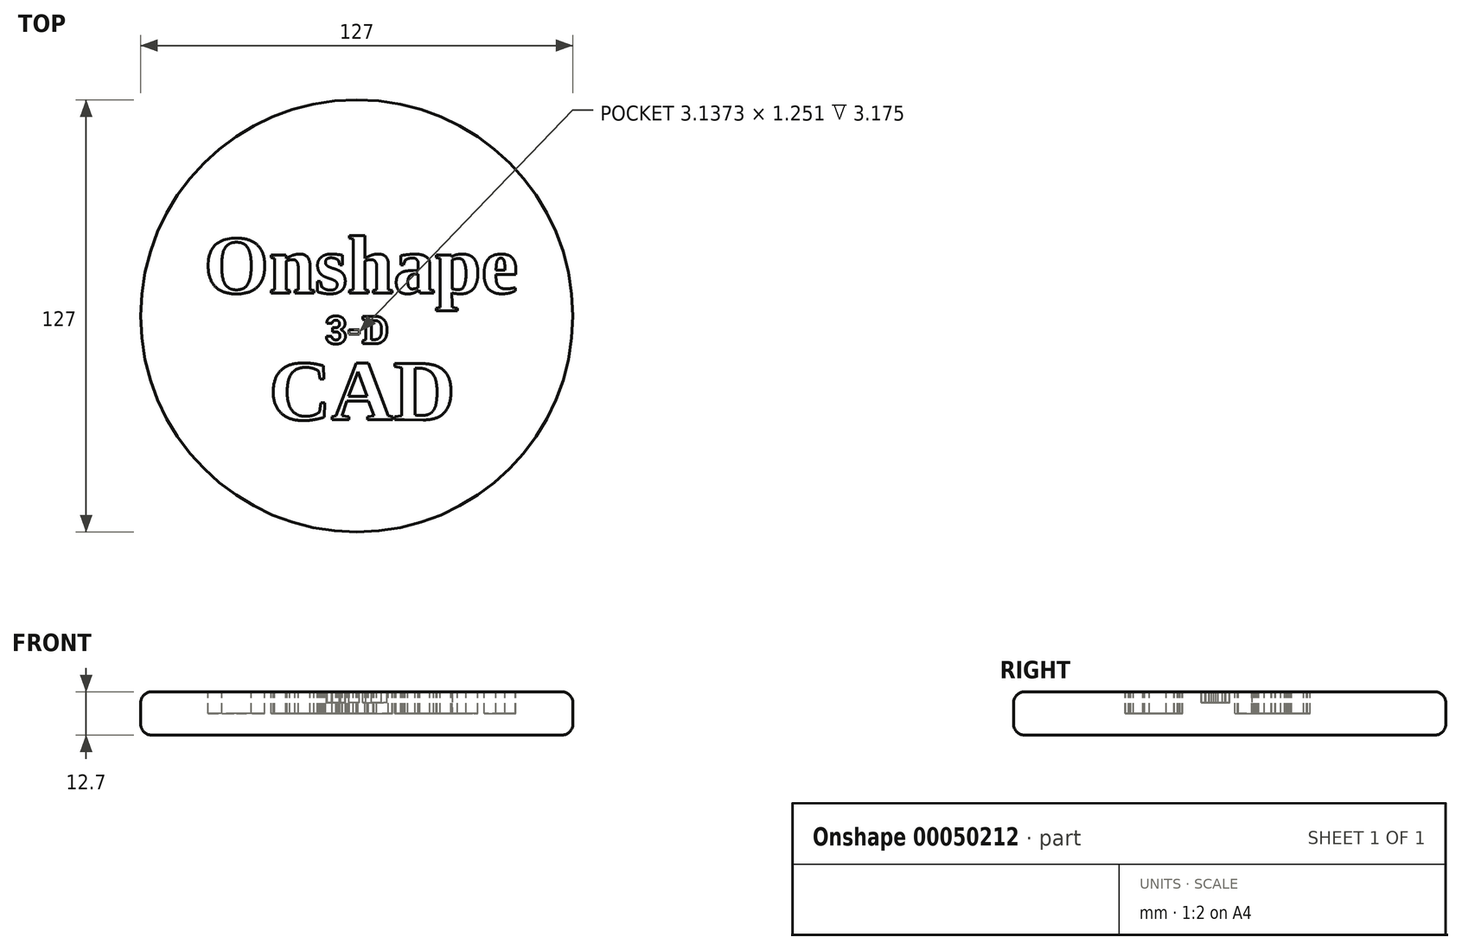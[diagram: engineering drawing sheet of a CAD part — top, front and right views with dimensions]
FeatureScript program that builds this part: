
annotation { "Feature Type Name" : "Feature", "Feature Type Description" : "" }
export const myFeature = defineFeature(function(context is Context, id is Id, definition is map)
    precondition{}
    {
        {
            var Q0;
            Q0=qCreatedBy(makeId("Top.planeOp"),FACE);
            var sketch = newSketch(context, id + "F0", { "sketchPlane" : qUnion([Q0])});
            skCircle(sketch, "E0", {"center": v(0, 0) * mm, "radius": 63.5 * mm});
            skSolve(sketch);
        }
        {
            var Q0;
            Q0=makeQuery(id+"F0.imprint","IMPRINT",FACE,{"disambiguationData":[TD([[makeQuery(id+"F0.imprint","IMPRINT",EDGE,{"derivedFrom":sQuery(id+"F0.wireOp",EDGE,"E0")}),1.0]])]});
            extrude(context, id + "F1", {"entities" : qUnion([Q0]), "depth" : 12.7 * mm});
        }
        {
            var Q0;
            Q0=makeQuery(id+"F1.opExtrude","CAP_FACE",FACE,{"disambiguationData":[OSD([sQuery(id+"F0.wireOp",EDGE,"E0")])],"isStart":false});
            var sketch = newSketch(context, id + "F2", { "sketchPlane" : qUnion([Q0])});
            skText(sketch, "E1", { "text": "Onshape", "fontName": "Tinos-Bold.ttf"});
            const initialGuessF2  = {"E1": [-0.04485, 0.0067, 1, 0, 0.01758]};
            skSetInitialGuess(sketch, initialGuessF2);
            skSolve(sketch);
        }
        {
            var Q0;
            Q0 = qSketchRegion(id + "F2", true);
            extrude(context, id + "F3", {"entities" : qUnion([Q0]), "operationType" : NewBodyOperationType.REMOVE, "oppositeDirection" : true, "depth" : 6.35 * mm});
        }
        {
            var Q0;
            {var subQ0=sQuery(id+"F0.wireOp",EDGE,"E0");Q0=makeQuery(id+"F3.boolean.opBoolean","SPLIT",FACE,{"disambiguationData":[TD([makeQuery(id+"F1.opExtrude","SWEPT_FACE",FACE,{"disambiguationData":[OSD([subQ0])]})])],"derivedFrom":makeQuery(id+"F1.opExtrude","CAP_FACE",FACE,{"disambiguationData":[OSD([subQ0])],"isStart":false})});}
            var sketch = newSketch(context, id + "F4", { "sketchPlane" : qUnion([Q0])});
            skText(sketch, "E2", { "text": "CAD", "fontName": "Tinos-Bold.ttf"});
            const initialGuessF4  = {"E2": [-0.02578, -0.03054, 1, 0, 0.01818]};
            skSetInitialGuess(sketch, initialGuessF4);
            skSolve(sketch);
        }
        {
            var Q0;
            Q0 = qSketchRegion(id + "F4", true);
            extrude(context, id + "F5", {"entities" : qUnion([Q0]), "operationType" : NewBodyOperationType.REMOVE, "oppositeDirection" : true, "depth" : 6.35 * mm});
        }
        {
            var Q0;
            Q0=makeQuery(id+"F1.opExtrude","CAP_EDGE",EDGE,{"disambiguationData":[OSD([sQuery(id+"F0.wireOp",EDGE,"E0")])],"isStart":false});
            var Q1;
            Q1=makeQuery(id+"F1.opExtrude","CAP_EDGE",EDGE,{"disambiguationData":[OSD([sQuery(id+"F0.wireOp",EDGE,"E0")])],"isStart":true});
            fillet(context, id + "F6", {"entities" : qUnion([Q0, Q1]), "radius" : 3.17 * mm, "tangentPropagation" : true, "allowEdgeOverflow" : false});
        }
        {
            var Q0;
            {var subQ68=sQuery(id+"F0.wireOp",EDGE,"E0");var subQ69=makeQuery(id+"F1.opExtrude","SWEPT_FACE",FACE,{"disambiguationData":[OSD([subQ68])]});Q0=makeQuery(id+"F5.boolean.opBoolean","SPLIT",FACE,{"disambiguationData":[TD([subQ69])],"derivedFrom":makeQuery(id+"F3.boolean.opBoolean","SPLIT",FACE,{"disambiguationData":[TD([subQ69])],"derivedFrom":makeQuery(id+"F1.opExtrude","CAP_FACE",FACE,{"disambiguationData":[OSD([subQ68])],"isStart":false})})});}
            var sketch = newSketch(context, id + "F7", { "sketchPlane" : qUnion([Q0])});
            skText(sketch, "E3", { "text": "3-D", "fontName": "RobotoSlab-Bold.ttf"});
            const initialGuessF7  = {"E3": [-0.00924, -0.0082, 1, 0, 0.0082]};
            skSetInitialGuess(sketch, initialGuessF7);
            skSolve(sketch);
        }
        {
            var Q0;
            Q0 = qSketchRegion(id + "F7", true);
            extrude(context, id + "F8", {"entities" : qUnion([Q0]), "operationType" : NewBodyOperationType.REMOVE, "oppositeDirection" : true, "depth" : 3.17 * mm});
        }
    });
